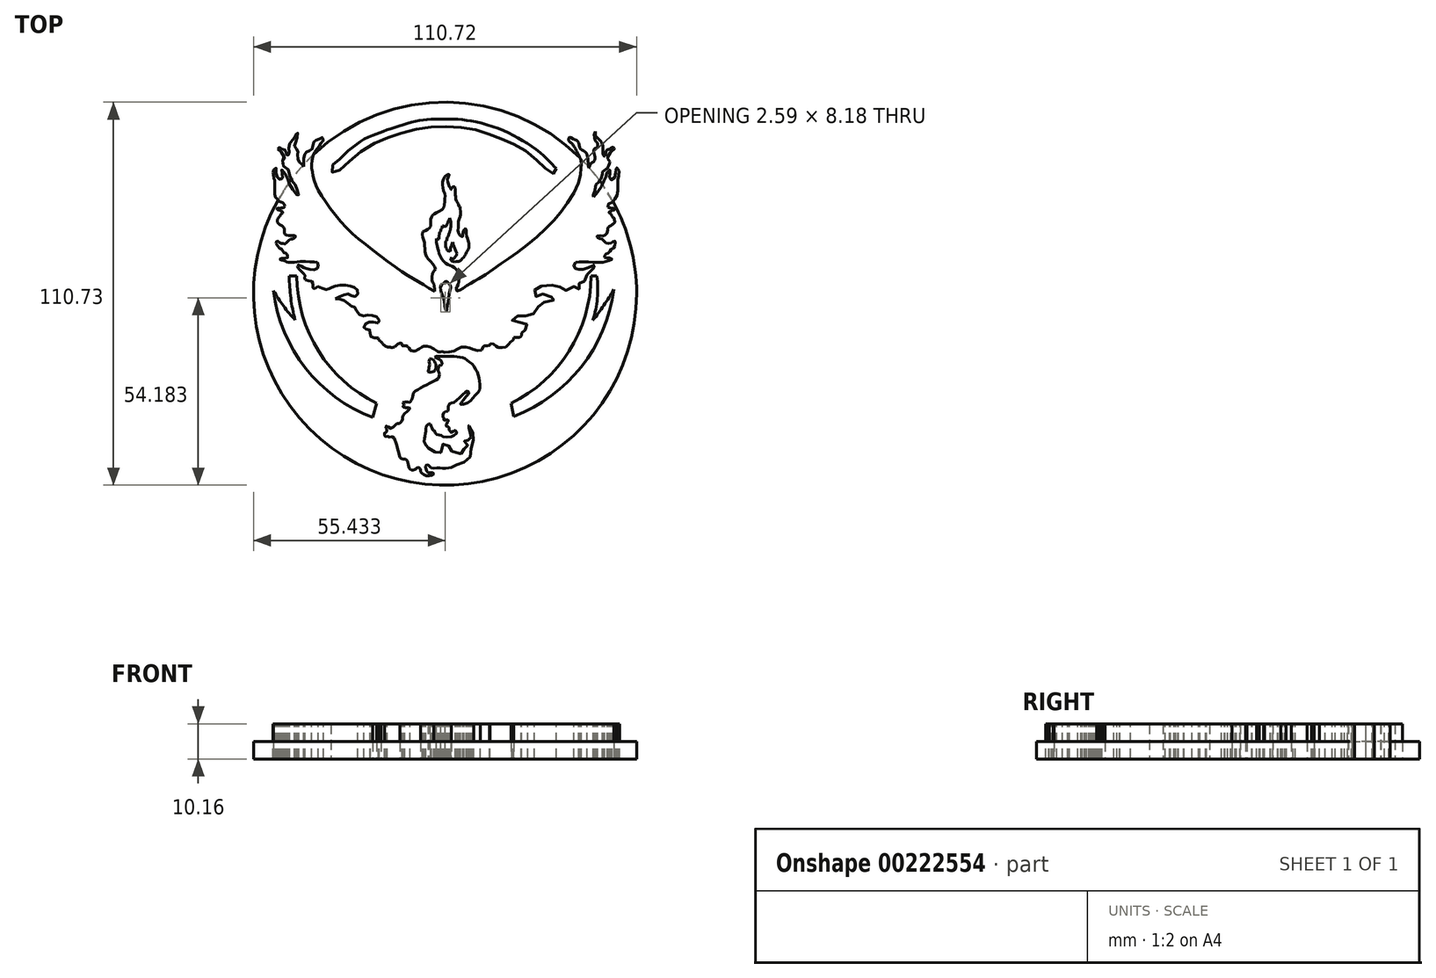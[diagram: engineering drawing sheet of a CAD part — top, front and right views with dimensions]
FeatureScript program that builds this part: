
annotation { "Feature Type Name" : "Feature", "Feature Type Description" : "" }
export const myFeature = defineFeature(function(context is Context, id is Id, definition is map)
    precondition{}
    {
        {
            var Q0;
            Q0=qCreatedBy(makeId("Top.planeOp"),FACE);
            var sketch = newSketch(context, id + "F0", { "sketchPlane" : qUnion([Q0])});
            skFitSpline(sketch, "E0", {"points": [v(-16.86, -5.52) * mm, v(-16.94, -4.58) * mm, v(-17.18, -3.24) * mm, v(-17.57, -2.77) * mm, v(-17.73, -1.5) * mm, v(-17.34, 0) * mm, v(-16.7, 0.77) * mm, v(-17.26, 2.2) * mm, v(-18.52, 3.53) * mm, v(-19.3, 4.55) * mm, v(-19.7, 5.97) * mm, v(-19.78, 7.54) * mm, v(-20.01, 9.12) * mm, v(-20.4, 10.3) * mm, v(-20.4, 11.71) * mm], "startDerivative": vector(-1.27, 14.06) * mm, "endDerivative": vector(1.69, 19.9) * mm});
            skFitSpline(sketch, "E1", {"points": [v(-20.4, 11.71) * mm, v(-18.83, 12.42) * mm, v(-18.12, 13.2) * mm, v(-18.04, 14.47) * mm, v(-17.89, 15.8) * mm, v(-17.42, 16.6) * mm, v(-16.08, 17.38) * mm, v(-14.35, 18.56) * mm, v(-14.03, 20.52) * mm, v(-13.95, 22.41) * mm, v(-14.5, 24.14) * mm, v(-14.58, 26.03) * mm], "startDerivative": vector(17.95, 6.85) * mm, "endDerivative": vector(1, 19.32) * mm});
            skFitSpline(sketch, "E2", {"points": [v(-14.58, 26.03) * mm, v(-14.35, 27.05) * mm, v(-13.54, 28) * mm, v(-12.72, 28.29) * mm, v(-12.8, 27.75) * mm, v(-13.23, 26.9) * mm, v(-13.17, 26.03) * mm, v(-12.8, 25.33) * mm, v(-12.78, 24.77) * mm, v(-12.4, 24.48) * mm, v(-12.3, 24.09) * mm, v(-12.07, 23.86) * mm, v(-11.87, 24.43) * mm, v(-11.6, 24.74) * mm, v(-11.17, 24.74) * mm, v(-10.97, 24.12) * mm, v(-11, 23.24) * mm, v(-10.89, 22.4) * mm, v(-10.8, 21.61) * mm, v(-10.8, 21.02) * mm, v(-10.47, 20.31) * mm, v(-9.96, 19.47) * mm, v(-9.85, 18.96) * mm, v(-9.48, 18.96) * mm], "startDerivative": vector(2.4, 19.07) * mm, "endDerivative": vector(13.83, 3.06) * mm});
            skFitSpline(sketch, "E3", {"points": [v(-9.48, 18.96) * mm, v(-9.48, 17.82) * mm, v(-9.48, 16.19) * mm, v(-9.9, 15.18) * mm, v(-10.1, 13.3) * mm, v(-10.1, 11.71) * mm, v(-9.48, 10.56) * mm, v(-8.8, 10.27) * mm, v(-8.8, 11.23) * mm, v(-8.36, 12.1) * mm, v(-8.02, 12.58) * mm, v(-7.78, 12.15) * mm, v(-7.78, 11.23) * mm, v(-7.54, 9.89) * mm, v(-7.2, 9.17) * mm], "startDerivative": vector(-0.48, -14.29) * mm, "endDerivative": vector(5.74, -10.35) * mm});
            skFitSpline(sketch, "E4", {"points": [v(-7.2, 9.17) * mm, v(-7.03, 8.35) * mm, v(-6.96, 7.49) * mm, v(-7.2, 6.6) * mm, v(-7.65, 5.86) * mm, v(-7.92, 5.3) * mm, v(-8.3, 4.6) * mm, v(-8.82, 3.99) * mm, v(-9.48, 3.35) * mm, v(-10.89, 3.01) * mm, v(-11.95, 3.25) * mm, v(-12.4, 3.97) * mm], "startDerivative": vector(2.2, -9.22) * mm, "endDerivative": vector(-4.07, 9.3) * mm});
            skFitSpline(sketch, "E5", {"points": [v(-12.4, 3.97) * mm, v(-11.32, 3.97) * mm, v(-10.84, 4.6) * mm, v(-10.47, 5.41) * mm, v(-10.99, 6.52) * mm, v(-11.51, 8.05) * mm, v(-11.66, 8.63) * mm], "startDerivative": vector(7.19, -1.15) * mm, "endDerivative": vector(-0.95, 3.88) * mm});
            skFitSpline(sketch, "E6", {"points": [v(-11.66, 8.63) * mm, v(-12.01, 7.92) * mm, v(-12.22, 7.4) * mm, v(-12.34, 6.78) * mm, v(-12.36, 6.25) * mm, v(-12.5, 6.03) * mm, v(-12.81, 6.1) * mm, v(-13.04, 6.13) * mm, v(-13.44, 6.8) * mm, v(-13.7, 7.44) * mm, v(-13.71, 8.3) * mm, v(-13.71, 8.87) * mm, v(-13.56, 8.98) * mm, v(-13.37, 9.47) * mm, v(-13.2, 9.97) * mm, v(-13.06, 10.22) * mm], "startDerivative": vector(-4.49, -8.8) * mm, "endDerivative": vector(2.8, 4.47) * mm});
            skFitSpline(sketch, "E7", {"points": [v(-13.06, 10.22) * mm, v(-12.55, 11.7) * mm, v(-12.27, 12.87) * mm, v(-12.27, 14.63) * mm, v(-12.55, 15.6) * mm], "startDerivative": vector(2.1, 5.8) * mm, "endDerivative": vector(-1.53, 4.03) * mm});
            skFitSpline(sketch, "E8", {"points": [v(-12.55, 15.6) * mm, v(-13.06, 14.53) * mm, v(-13.65, 13.29) * mm, v(-14.14, 13.29) * mm, v(-14.62, 13.32) * mm], "startDerivative": vector(-1.78, -3.18) * mm, "endDerivative": vector(-2.5, 0.02) * mm});
            skFitSpline(sketch, "E9", {"points": [v(-14.62, 13.32) * mm, v(-14.96, 12.42) * mm, v(-15.45, 11.45) * mm, v(-15.59, 10.66) * mm, v(-15.66, 9.93) * mm, v(-15.66, 9.62) * mm, v(-16.07, 9.59) * mm, v(-16.38, 9.66) * mm], "startDerivative": vector(-1.66, -5.03) * mm, "endDerivative": vector(-2.66, 0.75) * mm});
            skFitSpline(sketch, "E10", {"points": [v(-16.38, 9.66) * mm, v(-16.38, 8.95) * mm, v(-16.3, 8.08) * mm, v(-16.12, 7.17) * mm, v(-15.7, 5.74) * mm, v(-15, 3.97) * mm, v(-13.7, 2.58) * mm, v(-12.4, 1.88) * mm, v(-11.28, 1.42) * mm, v(-10.12, 0) * mm, v(-9.84, -0.78) * mm, v(-9.84, -2.49) * mm, v(-10.4, -4.2) * mm], "startDerivative": vector(-0.3, -11.43) * mm, "endDerivative": vector(-6.96, -16.94) * mm});
            skFitSpline(sketch, "E11", {"points": [v(-10.4, -4.2) * mm, v(-10.6, -4.39) * mm, v(-10.66, -4.94) * mm, v(-10.4, -5.38) * mm, v(-10.18, -5.49) * mm, v(-9.52, -5.12) * mm, v(-8.76, -4.67) * mm, v(-7.82, -3.98) * mm, v(-6.53, -3.27) * mm, v(-5.6, -2.64) * mm, v(-3.44, -1.53) * mm, v(1.05, 1.62) * mm, v(6.8, 5.57) * mm, v(14.8, 12.13) * mm, v(20.46, 18.5) * mm, v(24.77, 26.05) * mm, v(25.4, 30.18) * mm], "startDerivative": vector(-10.46, -6.9) * mm, "endDerivative": vector(1.76, 47.56) * mm});
            skFitSpline(sketch, "E12", {"points": [v(25.4, 30.18) * mm, v(25.4, 32.23) * mm, v(24.15, 34.94) * mm, v(23.08, 36.75) * mm, v(21.78, 38.05) * mm], "startDerivative": vector(1.08, 8.26) * mm, "endDerivative": vector(-6.03, 5.72) * mm});
            skFitSpline(sketch, "E13", {"points": [v(21.78, 38.05) * mm, v(22.08, 39.01) * mm, v(23.23, 38.42) * mm, v(24.3, 38.05) * mm, v(24.82, 37.12) * mm, v(25.08, 35.83) * mm, v(25.93, 35.16) * mm, v(26.86, 34.53) * mm, v(27.26, 33.34) * mm, v(27.49, 31.94) * mm, v(27.52, 30.94) * mm, v(27.7, 30.18) * mm], "startDerivative": vector(1.63, 15.2) * mm, "endDerivative": vector(3.06, -9.7) * mm});
            skFitSpline(sketch, "E14", {"points": [v(27.7, 30.18) * mm, v(28.26, 31.42) * mm, v(28.97, 31.86) * mm, v(29.34, 32.5) * mm, v(29.38, 33.38) * mm, v(29.15, 34.27) * mm, v(29.08, 34.94) * mm, v(29.38, 35.79) * mm, v(30, 35.9) * mm, v(30.26, 36.57) * mm, v(30.04, 37.5) * mm, v(29.52, 38.05) * mm, v(29.23, 39.68) * mm, v(29.6, 40.68) * mm], "startDerivative": vector(4.58, 15.51) * mm, "endDerivative": vector(5.9, 10.64) * mm});
            skFitSpline(sketch, "E15", {"points": [v(29.6, 40.68) * mm, v(29.6, 39.57) * mm, v(30.26, 38.71) * mm, v(30.93, 38.05) * mm, v(31.6, 37.01) * mm, v(31.75, 35.64) * mm, v(31.67, 34.82) * mm, v(31.75, 34.34) * mm, v(31.93, 33.64) * mm, v(32.3, 33.53) * mm], "startDerivative": vector(-1.31, -9.25) * mm, "endDerivative": vector(5.74, -0.16) * mm});
            skFitSpline(sketch, "E16", {"points": [v(32.3, 33.53) * mm, v(32.52, 34.2) * mm, v(32.64, 34.92) * mm, v(32.91, 35.39) * mm, v(33.38, 35.4) * mm, v(33.93, 35.58) * mm, v(34.15, 35.97) * mm, v(34.67, 36.1) * mm, v(35.08, 35.73) * mm, v(34.68, 35.3) * mm, v(33.93, 34.7) * mm, v(33.4, 33.74) * mm, v(33.05, 33.15) * mm, v(33.17, 32.67) * mm, v(33.6, 32.22) * mm, v(33.74, 31.64) * mm, v(33.48, 30.97) * mm, v(33.1, 30.38) * mm, v(33.08, 29.95) * mm, v(32.77, 29.92) * mm, v(32.3, 29.5) * mm, v(31.6, 28.97) * mm], "startDerivative": vector(4.9, 12.98) * mm, "endDerivative": vector(-13.3, -8.7) * mm});
            skFitSpline(sketch, "E17", {"points": [v(31.6, 28.97) * mm, v(31.6, 28.25) * mm, v(31.22, 27.1) * mm, v(30.93, 26.64) * mm, v(30.48, 26.05) * mm, v(29.74, 25.3) * mm, v(29.63, 24.77) * mm, v(29.46, 23.75) * mm, v(29.26, 23.07) * mm, v(28.95, 22.13) * mm, v(29, 21.77) * mm], "startDerivative": vector(0.7, -6.71) * mm, "endDerivative": vector(1.6, -4.57) * mm});
            skFitSpline(sketch, "E18", {"points": [v(29, 21.77) * mm, v(29.98, 22.85) * mm, v(31.01, 24.31) * mm, v(31.82, 25.62) * mm, v(32, 26.42) * mm, v(32.38, 27.1) * mm, v(32.72, 27.98) * mm, v(32.81, 28.7) * mm, v(33.16, 28.97) * mm, v(33.56, 29.47) * mm, v(33.87, 29.47) * mm, v(33.84, 29.16) * mm, v(33.8, 28.6) * mm, v(33.68, 27.92) * mm, v(33.68, 27.17) * mm, v(33.75, 26.7) * mm, v(34.27, 26.74) * mm, v(34.74, 27.2) * mm, v(35.18, 27.39) * mm, v(35.4, 28.29) * mm, v(35.4, 29.1) * mm, v(35.58, 29.4) * mm, v(35.42, 30.1) * mm, v(35.46, 30.43) * mm, v(35.83, 30.03) * mm, v(36.1, 29.4) * mm, v(36.42, 29.13) * mm, v(36.42, 28.2) * mm, v(36.17, 27.6) * mm, v(36.17, 26.9) * mm, v(35.92, 26.49) * mm, v(35.98, 25.46) * mm, v(35.98, 24.31) * mm, v(36.02, 22.76) * mm, v(35.8, 22.13) * mm, v(35.77, 21.77) * mm, v(35.27, 21.17) * mm, v(34.7, 20.7) * mm, v(34.5, 20.27) * mm, v(34, 20.24) * mm, v(33.28, 19.74) * mm, v(33.03, 19.24) * mm, v(33.16, 18.75) * mm], "startDerivative": vector(28.84, 29.63) * mm, "endDerivative": vector(9.8, -24.72) * mm});
            skFitSpline(sketch, "E19", {"points": [v(33.16, 18.75) * mm, v(33.6, 18.61) * mm, v(34.2, 18.5) * mm, v(34.76, 18.52) * mm, v(35.12, 18.48) * mm, v(35.16, 18.26) * mm, v(34.77, 17.9) * mm, v(34.42, 17.88) * mm, v(34.13, 17.7) * mm, v(33.72, 17.5) * mm, v(33.54, 17.27) * mm, v(33.64, 17.06) * mm, v(33.98, 16.93) * mm, v(34.18, 16.7) * mm], "startDerivative": vector(5.08, -1.62) * mm, "endDerivative": vector(2.28, -3.99) * mm});
            skFitSpline(sketch, "E20", {"points": [v(34.18, 16.7) * mm, v(34.36, 16.24) * mm, v(34.41, 16) * mm, v(34.76, 15.72) * mm, v(35.07, 15.48) * mm, v(35.07, 14.92) * mm, v(35.27, 14.5) * mm, v(34.76, 14.02) * mm, v(34.18, 13.51) * mm, v(33.49, 13.15) * mm, v(33.16, 12.61) * mm, v(33.16, 12.05) * mm], "startDerivative": vector(2.74, -5.6) * mm, "endDerivative": vector(0.66, -6.02) * mm});
            skFitSpline(sketch, "E21", {"points": [v(33.16, 12.05) * mm, v(32.7, 10.9) * mm, v(31.8, 10.52) * mm, v(30.7, 10.56) * mm, v(29.95, 10.33) * mm, v(30.56, 9.8) * mm, v(31.51, 9.52) * mm, v(32.27, 8.76) * mm, v(33.16, 8.3) * mm, v(34.18, 8.48) * mm, v(34.76, 8.86) * mm, v(35.27, 8.95) * mm, v(35.27, 8.05) * mm, v(34.76, 6.92) * mm, v(34.18, 6.68) * mm, v(33.6, 5.78) * mm, v(32.7, 5.35) * mm, v(32.27, 4.88) * mm, v(32.22, 4.17) * mm], "startDerivative": vector(-4.75, -20.24) * mm, "endDerivative": vector(0.74, -15.16) * mm});
            skFitSpline(sketch, "E22", {"points": [v(32.22, 4.17) * mm, v(32.64, 4.3) * mm, v(32.89, 4.12) * mm, v(33.47, 4.12) * mm, v(34.18, 4.03) * mm, v(34.37, 3.74) * mm, v(33.64, 3.34) * mm, v(32.85, 3.16) * mm, v(32.34, 2.88) * mm, v(31.32, 2.82) * mm, v(29.46, 2.84) * mm, v(28, 2.95) * mm, v(26.79, 2.97) * mm, v(25.47, 2.99) * mm, v(24.26, 2.93) * mm, v(23.63, 2.63) * mm, v(23.32, 1.74) * mm, v(23.7, 1.07) * mm, v(24.7, 0.75) * mm, v(26.01, 0.86) * mm, v(27.16, 1.13) * mm, v(28.08, 1.57) * mm, v(28.81, 1.86) * mm, v(29.17, 2) * mm, v(29.19, 1.44) * mm, v(28.46, 0.6) * mm, v(27.96, 0) * mm, v(27.29, -0.4) * mm, v(27.1, -0.77) * mm], "startDerivative": vector(17.9, 9.8) * mm, "endDerivative": vector(-4.25, -15.98) * mm});
            skFitSpline(sketch, "E23", {"points": [v(27.1, -0.77) * mm, v(27.1, -1.72) * mm, v(26.67, -2.35) * mm, v(25.57, -2.78) * mm, v(25.04, -2.68) * mm, v(24.84, -3.4) * mm, v(24.75, -4.27) * mm, v(25.08, -4.66) * mm, v(24.41, -4.95) * mm, v(23.98, -4.22) * mm, v(23.4, -4.13) * mm, v(22.3, -5.04) * mm, v(21.14, -5.28) * mm, v(20.03, -4.8) * mm, v(19.55, -4.42) * mm, v(18.44, -3.89) * mm, v(17.58, -3.8) * mm, v(16.18, -3.74) * mm, v(14.16, -3.98) * mm, v(12.9, -4.37) * mm, v(12.1, -4.95) * mm, v(11.95, -6.05) * mm, v(12.1, -6.63) * mm, v(12.62, -7.16) * mm, v(13.73, -6.73) * mm, v(14.3, -6.34) * mm, v(15.6, -6.53) * mm, v(17.2, -7.4) * mm, v(18.25, -8.03) * mm, v(16.85, -8.07) * mm, v(15.46, -8.31) * mm, v(14.16, -9.13) * mm, v(13.68, -9.57) * mm, v(12.96, -10.1) * mm, v(12.23, -11.1) * mm, v(11.6, -12.07) * mm, v(10.21, -12.65) * mm, v(9.25, -12.7) * mm, v(8.05, -12.5) * mm, v(7.04, -12.74) * mm, v(6.36, -13.32) * mm, v(5.54, -13.7) * mm, v(5.93, -14.72) * mm, v(6.9, -14.52) * mm, v(8.2, -14.38) * mm, v(9.5, -14.81) * mm, v(10.02, -15.92) * mm, v(9.88, -16.54) * mm, v(8.87, -16.64) * mm, v(8.1, -16.69) * mm, v(8.24, -17.6) * mm], "startDerivative": vector(4.98, -52.78) * mm, "endDerivative": vector(20.93, -60.42) * mm});
            skFitSpline(sketch, "E24", {"points": [v(8.24, -17.6) * mm, v(8.24, -18.16) * mm, v(7.84, -18.73) * mm, v(6.85, -18.91) * mm, v(5.93, -18.89) * mm], "startDerivative": vector(0.31, -2.6) * mm, "endDerivative": vector(-3.27, 0.16) * mm});
            skFitSpline(sketch, "E25", {"points": [v(5.93, -18.89) * mm, v(5.93, -19.49) * mm, v(5.26, -19.85) * mm, v(4.82, -20.48) * mm, v(4.17, -21.18) * mm, v(3.28, -21.83) * mm, v(2.26, -21.83) * mm, v(1.35, -21.8) * mm, v(0.78, -21.34) * mm, v(0.26, -20.87) * mm, v(-0.5, -20.69) * mm, v(-1, -20.74) * mm, v(-0.97, -21.1) * mm, v(-1.3, -21.34) * mm, v(-2.2, -21.29) * mm, v(-2.61, -21.36) * mm, v(-2.8, -21.62) * mm, v(-3.03, -21.7) * mm, v(-3.38, -22.61) * mm, v(-4.85, -22.61) * mm, v(-6.25, -22.23) * mm, v(-6.94, -21.85) * mm, v(-8.47, -21.6) * mm, v(-9.61, -21.79) * mm, v(-10.82, -22.55) * mm, v(-12.54, -23.06) * mm, v(-13.94, -23.18) * mm], "startDerivative": vector(5.13, -21.26) * mm, "endDerivative": vector(-27.28, -1.54) * mm});
            skFitSpline(sketch, "E26", {"points": [v(18.24, 30) * mm, v(16.85, 31.38) * mm, v(13.79, 34.37) * mm, v(8.24, 38.17) * mm, v(2.1, 41.31) * mm, v(-5.35, 43.5) * mm, v(-10.18, 44.24) * mm], "startDerivative": vector(-12.55, 12.25) * mm, "endDerivative": vector(-27.98, 3.35) * mm});
            skFitSpline(sketch, "E27", {"points": [v(-10.18, 44.24) * mm, v(-17.52, 44.24) * mm, v(-21.6, 43.8) * mm, v(-26.13, 42.55) * mm, v(-30.4, 41.23) * mm, v(-33.87, 39.87) * mm, v(-38.43, 37.82) * mm], "startDerivative": vector(-38.77, 0.5) * mm, "endDerivative": vector(-27.3, -16.6) * mm});
            skFitSpline(sketch, "E28", {"points": [v(-38.43, 37.82) * mm, v(-43.44, 33.67) * mm, v(-45.42, 31.68) * mm, v(-46.83, 30.18) * mm, v(-46.27, 28.67) * mm, v(-43.81, 29.99) * mm, v(-39.57, 33.76) * mm, v(-33.15, 37.82) * mm, v(-27.4, 39.9) * mm, v(-20.7, 41.59) * mm, v(-13.91, 42.06) * mm, v(-7.12, 41.59) * mm, v(-1.27, 39.99) * mm, v(3.92, 37.82) * mm, v(8.92, 35.46) * mm, v(13.35, 31.68) * mm, v(16.18, 29.14) * mm, v(17.78, 28.57) * mm, v(18.24, 30) * mm], "startDerivative": vector(-87.21, -57.5) * mm, "endDerivative": vector(6.34, 58.2) * mm});
            skFitSpline(sketch, "E29", {"points": [v(-13.94, -23.18) * mm, v(-14.86, -23) * mm, v(-15.8, -23) * mm, v(-16.37, -22.69) * mm, v(-17.35, -22.09) * mm, v(-18.36, -21.6) * mm, v(-19.4, -21.43) * mm, v(-19.9, -21.4) * mm, v(-20.75, -21.86) * mm, v(-21.73, -22.39) * mm, v(-22.69, -22.77) * mm, v(-23.53, -22.72) * mm], "startDerivative": vector(-9.74, 2.84) * mm, "endDerivative": vector(-9.64, 1.67) * mm});
            skFitSpline(sketch, "E30", {"points": [v(-23.53, -22.72) * mm, v(-24.1, -22.54) * mm, v(-24.18, -22.11) * mm, v(-24.3, -21.77) * mm, v(-24.64, -21.77) * mm, v(-24.69, -21.45) * mm, v(-24.92, -21.34) * mm, v(-25.8, -21.35) * mm, v(-26.34, -21.26) * mm, v(-26.29, -20.81) * mm], "startDerivative": vector(-5.43, 0.74) * mm, "endDerivative": vector(1.54, 4.76) * mm});
            skFitSpline(sketch, "E31", {"points": [v(-26.29, -20.81) * mm, v(-26.78, -20.58) * mm, v(-27.8, -21) * mm, v(-28.53, -21.63) * mm, v(-29.55, -21.75) * mm, v(-30.87, -21.54) * mm, v(-31.84, -20.81) * mm, v(-32.43, -20.02) * mm], "startDerivative": vector(-4.1, 3.18) * mm, "endDerivative": vector(-3.81, 5.64) * mm});
            skFitSpline(sketch, "E32", {"points": [v(-32.43, -20.02) * mm, v(-33.07, -19.58) * mm, v(-33.1, -19) * mm], "startDerivative": vector(-1.5, 0.71) * mm, "endDerivative": vector(0.19, 1.34) * mm});
            skFitSpline(sketch, "E33", {"points": [v(-33.1, -19) * mm, v(-34.57, -19) * mm, v(-35.54, -18.42) * mm, v(-35.48, -17.03) * mm, v(-35.96, -16.54) * mm, v(-37.28, -16.33) * mm, v(-37.21, -15.3) * mm, v(-36.1, -14.46) * mm, v(-34.85, -14.46) * mm, v(-33.1, -14.67) * mm, v(-33.1, -13.56) * mm, v(-34.5, -12.58) * mm, v(-36.1, -12.44) * mm, v(-37.9, -12.65) * mm, v(-39.3, -11.54) * mm, v(-39.99, -10.15) * mm, v(-40.82, -9.87) * mm, v(-42.42, -8.7) * mm, v(-43.8, -7.93) * mm, v(-45.62, -7.72) * mm], "startDerivative": vector(-27.39, -2.24) * mm, "endDerivative": vector(-31.84, 1.41) * mm});
            skFitSpline(sketch, "E34", {"points": [v(-45.62, -7.72) * mm, v(-43.4, -6.68) * mm, v(-41.66, -6.33) * mm, v(-40.34, -7.03) * mm, v(-39.3, -6.6) * mm, v(-39.3, -5.01) * mm, v(-40.82, -4.18) * mm, v(-43.05, -3.76) * mm, v(-45.62, -4.04) * mm, v(-46.93, -4.53) * mm, v(-47.7, -4.94) * mm, v(-49.02, -4.94) * mm, v(-50.9, -4.18) * mm, v(-51.87, -4.94) * mm, v(-52.07, -3.7) * mm, v(-52.28, -2.72) * mm, v(-53.19, -2.58) * mm, v(-54.23, -2.23) * mm], "startDerivative": vector(29.87, 14.57) * mm, "endDerivative": vector(-19.98, 8.99) * mm});
            skFitSpline(sketch, "E35", {"points": [v(-54.23, -2.23) * mm, v(-54.47, -1.81) * mm, v(-54.43, -1.26) * mm, v(-54.5, -0.57) * mm, v(-54.89, -0.33) * mm, v(-55.25, 0) * mm, v(-55.67, 0.46) * mm, v(-56.26, 1.05) * mm, v(-56.54, 1.6) * mm, v(-56.47, 2.06) * mm, v(-55.63, 1.83) * mm, v(-54.83, 1.3) * mm, v(-54.03, 1.03) * mm, v(-52.77, 0.78) * mm, v(-51.11, 0.9) * mm, v(-50.56, 1.87) * mm, v(-50.9, 2.84) * mm, v(-52.16, 3) * mm, v(-54.03, 3.05) * mm, v(-56.24, 3.05) * mm, v(-56.98, 2.82) * mm, v(-58.68, 2.82) * mm], "startDerivative": vector(-9.07, 11.9) * mm, "endDerivative": vector(-30.21, 1.95) * mm});
            skFitSpline(sketch, "E36", {"points": [v(-58.68, 2.82) * mm, v(-59.48, 2.93) * mm, v(-60.08, 3.15) * mm, v(-60.47, 3.32) * mm, v(-61.26, 3.5) * mm, v(-61.57, 3.65) * mm, v(-61.49, 3.9) * mm, v(-60.87, 3.97) * mm, v(-60.17, 4) * mm, v(-59.85, 4.19) * mm, v(-59.45, 4.16) * mm, v(-59.43, 4.81) * mm, v(-59.74, 5.29) * mm, v(-60.46, 5.67) * mm, v(-60.78, 5.95) * mm, v(-60.96, 6.39) * mm, v(-61.3, 6.78) * mm, v(-61.8, 6.84) * mm, v(-61.95, 7.16) * mm, v(-62.13, 7.37) * mm, v(-62.26, 7.5) * mm], "startDerivative": vector(-12.7, 1.25) * mm, "endDerivative": vector(-3.95, 4.14) * mm});
            skFitSpline(sketch, "E37", {"points": [v(-62.26, 7.5) * mm, v(-62.4, 7.82) * mm, v(-62.67, 8.06) * mm, v(-62.71, 8.46) * mm, v(-62.6, 8.93) * mm, v(-62.07, 8.89) * mm, v(-61.59, 8.45) * mm, v(-61.1, 8.26) * mm, v(-60.71, 8.3) * mm, v(-60.23, 8.16) * mm, v(-59.62, 8.64) * mm, v(-58.83, 9.4) * mm, v(-58.35, 9.57) * mm, v(-57.9, 9.6) * mm, v(-57.3, 10.04) * mm, v(-57.12, 10.49) * mm, v(-57.99, 10.64) * mm, v(-59.02, 10.64) * mm, v(-59.72, 10.65) * mm, v(-60.12, 10.9) * mm, v(-60.32, 11.33) * mm, v(-60.36, 11.96) * mm, v(-60.36, 12.31) * mm, v(-60.4, 12.56) * mm, v(-60.54, 12.95) * mm], "startDerivative": vector(-3.04, 10.53) * mm, "endDerivative": vector(-4.1, 11.48) * mm});
            skFitSpline(sketch, "E38", {"points": [v(-60.54, 12.95) * mm, v(-61.04, 13.4) * mm, v(-61.79, 13.8) * mm, v(-62.19, 14.21) * mm, v(-62.38, 14.4) * mm, v(-62.4, 14.66) * mm, v(-62.4, 15.04) * mm, v(-62.24, 15.45) * mm, v(-61.88, 15.85) * mm, v(-61.61, 16.08) * mm], "startDerivative": vector(-3.27, 3.65) * mm, "endDerivative": vector(2.56, 2.25) * mm});
            skFitSpline(sketch, "E39", {"points": [v(-61.61, 16.08) * mm, v(-61.61, 16.44) * mm, v(-61.27, 16.8) * mm, v(-60.92, 16.97) * mm, v(-60.79, 17.34) * mm, v(-61.12, 17.6) * mm, v(-61.42, 17.72) * mm, v(-61.61, 17.91) * mm, v(-62.05, 17.9) * mm, v(-62.45, 18.2) * mm, v(-62.32, 18.5) * mm, v(-61.61, 18.5) * mm, v(-60.96, 18.6) * mm, v(-60.4, 18.72) * mm, v(-60.29, 19.3) * mm, v(-60.54, 19.8) * mm, v(-61.08, 20.18) * mm, v(-61.48, 20.3) * mm, v(-61.9, 20.55) * mm], "startDerivative": vector(-1.38, 7.32) * mm, "endDerivative": vector(-7.32, 5.24) * mm});
            skFitSpline(sketch, "E40", {"points": [v(-61.9, 20.55) * mm, v(-62.2, 20.92) * mm, v(-62.63, 21.4) * mm, v(-62.88, 21.55) * mm, v(-63, 21.9) * mm], "startDerivative": vector(-1.14, 1.28) * mm, "endDerivative": vector(-0.26, 1.84) * mm});
            skFitSpline(sketch, "E41", {"points": [v(-63, 21.9) * mm, v(-63.1, 22.2) * mm, v(-63.17, 23.46) * mm, v(-63.16, 25.51) * mm, v(-63.1, 26.48) * mm, v(-63.26, 26.72) * mm, v(-63.36, 27.2) * mm, v(-63.47, 27.84) * mm, v(-63.56, 28.24) * mm, v(-63.56, 29.04) * mm, v(-63.35, 29.6) * mm], "startDerivative": vector(-1.95, 3.68) * mm, "endDerivative": vector(2.85, 5.49) * mm});
            skFitSpline(sketch, "E42", {"points": [v(-63.35, 29.6) * mm, v(-62.97, 30.26) * mm, v(-62.72, 30.33) * mm, v(-62.77, 29.6) * mm, v(-62.63, 29.04) * mm, v(-62.7, 28.24) * mm, v(-62.38, 27.84) * mm, v(-62.4, 27.48) * mm, v(-61.9, 27.43) * mm, v(-61.9, 27.16) * mm, v(-61.53, 26.72) * mm, v(-60.9, 26.72) * mm, v(-60.92, 27.33) * mm, v(-60.87, 27.84) * mm, v(-60.94, 28.24) * mm, v(-61.02, 29.04) * mm, v(-61.29, 29.26) * mm, v(-61.11, 29.6) * mm, v(-60.4, 29.04) * mm, v(-59.97, 28.04) * mm, v(-59.58, 27.11) * mm, v(-59.26, 26.65) * mm, v(-59.29, 26.09) * mm, v(-58.8, 25.43) * mm, v(-58.26, 24.4) * mm, v(-57.4, 23.26) * mm, v(-56.75, 22.38) * mm, v(-56.29, 21.9) * mm, v(-56.16, 22.18) * mm, v(-56.46, 22.57) * mm, v(-56.6, 23.38) * mm, v(-56.8, 24.18) * mm, v(-56.94, 24.99) * mm, v(-57.43, 25.55) * mm, v(-58.04, 26.35) * mm, v(-58.43, 26.62) * mm, v(-58.87, 27.84) * mm, v(-58.82, 28.62) * mm, v(-59.26, 29.6) * mm, v(-60.14, 30.11) * mm, v(-60.7, 30.87) * mm, v(-61.04, 31.72) * mm, v(-60.65, 32.48) * mm, v(-60.29, 33.06) * mm, v(-60.65, 33.7) * mm, v(-60.94, 34.3) * mm, v(-61.43, 34.82) * mm, v(-61.9, 35.23) * mm, v(-62.21, 35.55) * mm], "startDerivative": vector(14.73, 35.5) * mm, "endDerivative": vector(-18.28, 18.47) * mm});
            skFitSpline(sketch, "E43", {"points": [v(-62.21, 35.55) * mm, v(-62.1, 35.92) * mm, v(-61.71, 36.06) * mm, v(-61.11, 35.76) * mm, v(-61.11, 35.55) * mm, v(-60.4, 35.45) * mm, v(-59.88, 35) * mm, v(-59.85, 34.41) * mm, v(-59.62, 34.08) * mm, v(-59.57, 33.7) * mm, v(-59.22, 33.7) * mm, v(-59.12, 34.18) * mm, v(-58.96, 34.53) * mm, v(-59.05, 35.03) * mm, v(-59.07, 36.49) * mm, v(-58.67, 37.4) * mm, v(-57.94, 38.23) * mm, v(-57.4, 38.89) * mm, v(-56.93, 39.45) * mm, v(-56.9, 40.16) * mm, v(-56.6, 40.32) * mm, v(-56.56, 39.45) * mm, v(-56.74, 38.3) * mm, v(-57.3, 37.2) * mm, v(-57.45, 36.27) * mm, v(-57.05, 35.83) * mm, v(-56.58, 35.55) * mm, v(-56.34, 34.44) * mm, v(-56.48, 34.08) * mm, v(-56.48, 32.95) * mm, v(-56.34, 32.32) * mm, v(-55.92, 31.73) * mm, v(-55.61, 31.59) * mm, v(-55.21, 30.9) * mm, v(-54.77, 30.55) * mm], "startDerivative": vector(2.06, 18.3) * mm, "endDerivative": vector(17.48, -9.47) * mm});
            skFitSpline(sketch, "E44", {"points": [v(-54.77, 30.55) * mm, v(-54.77, 32.2) * mm, v(-54.39, 34.16) * mm, v(-53.68, 34.96) * mm, v(-52.5, 35.45) * mm, v(-52.06, 36.6) * mm, v(-51.63, 37.88) * mm, v(-50.62, 38.3) * mm, v(-49.4, 38.96) * mm, v(-49.2, 38.49) * mm, v(-49.02, 38.16) * mm, v(-49.63, 37.52) * mm, v(-50.39, 36.35) * mm, v(-51.33, 35.17) * mm, v(-52.15, 33.38) * mm, v(-52.53, 31.24) * mm, v(-52.39, 29.6) * mm, v(-52.06, 27.84) * mm], "startDerivative": vector(-0.91, 23.81) * mm, "endDerivative": vector(5.14, -26.17) * mm});
            skFitSpline(sketch, "E45", {"points": [v(-52.06, 27.84) * mm, v(-51.05, 24.69) * mm, v(-48.02, 19.8) * mm, v(-42.26, 12.67) * mm, v(-34.73, 6.31) * mm, v(-26.13, 0) * mm, v(-21.53, -2.88) * mm, v(-16.86, -5.52) * mm], "startDerivative": vector(7.65, -30.8) * mm, "endDerivative": vector(37.83, -21.2) * mm});
            skFitSpline(sketch, "E46", {"points": [v(-13.52, -11.49) * mm, v(-13.86, -10.23) * mm, v(-14.03, -9.6) * mm, v(-14.03, -9.14) * mm, v(-14.26, -7.82) * mm, v(-14.55, -7.02) * mm, v(-14.9, -5.99) * mm, v(-15.12, -5.52) * mm, v(-15.18, -3.98) * mm, v(-14.43, -3.27) * mm, v(-13.8, -2.67) * mm, v(-12.94, -3.27) * mm, v(-12.26, -4.18) * mm, v(-12.54, -5.52) * mm, v(-12.89, -7.94) * mm, v(-13.29, -9.94) * mm, v(-13.52, -11.49) * mm]});
            skArc(sketch, "E47", {"start": v(-63.5, -5.43) * mm, "mid": v(-54.23, -27.74) * mm, "end": v(-34.77, -42.05) * mm});
            skArc(sketch, "E48", {"start": v(-63.5, -5.43) * mm, "mid": v(-60.6, -9.78) * mm, "end": v(-57.27, -13.82) * mm});
            skArc(sketch, "E49", {"start": v(-58.92, -1.11) * mm, "mid": v(-58.5, -7.52) * mm, "end": v(-57.27, -13.82) * mm});
            skLineSegment(sketch, "E50", {"start": v(-58.92, -1.11) * mm, "end": v(-56.76, -1.11) * mm});
            skLineSegment(sketch, "E51", {"start": v(-34.77, -42.05) * mm, "end": v(-33.62, -37.98) * mm});
            skArc(sketch, "E52", {"start": v(-56.76, -1.11) * mm, "mid": v(-50.45, -22.85) * mm, "end": v(-33.62, -37.98) * mm});
            skArc(sketch, "E53", {"start": v(5.15, -37.98) * mm, "mid": v(21.96, -22.83) * mm, "end": v(28.33, -1.11) * mm});
            skLineSegment(sketch, "E54", {"start": v(28.33, -1.11) * mm, "end": v(29.99, -1.11) * mm});
            skArc(sketch, "E55", {"start": v(28.83, -13.93) * mm, "mid": v(30.12, -7.58) * mm, "end": v(29.99, -1.11) * mm});
            skArc(sketch, "E56", {"start": v(28.83, -13.93) * mm, "mid": v(32, -9.6) * mm, "end": v(34.87, -5.07) * mm});
            skArc(sketch, "E57", {"start": v(5.98, -41.74) * mm, "mid": v(25.47, -27.38) * mm, "end": v(34.87, -5.07) * mm});
            skLineSegment(sketch, "E58", {"start": v(5.15, -37.98) * mm, "end": v(5.98, -41.74) * mm});
            skFitSpline(sketch, "E59", {"points": [v(-16.97, -24.55) * mm, v(-16.2, -24.38) * mm, v(-14.83, -24.34) * mm, v(-12.62, -24.34) * mm, v(-10.76, -24.38) * mm, v(-9.18, -24.7) * mm, v(-8.2, -24.87) * mm, v(-7.43, -25.57) * mm, v(-6.1, -26.48) * mm, v(-5.19, -27.88) * mm, v(-4.56, -29.04) * mm, v(-4.03, -30.65) * mm, v(-3.82, -32.2) * mm, v(-3.85, -33.98) * mm, v(-4.45, -34.9) * mm], "startDerivative": vector(13.75, 3.93) * mm, "endDerivative": vector(-11.64, -12.72) * mm});
            skFitSpline(sketch, "E60", {"points": [v(-4.45, -34.9) * mm, v(-5.88, -36.5) * mm, v(-7.34, -37.75) * mm, v(-9.4, -38.28) * mm, v(-8.8, -37.29) * mm, v(-7.6, -35.77) * mm, v(-7, -34.9) * mm, v(-7.27, -34.44) * mm, v(-8.2, -34.9) * mm, v(-10.24, -36.83) * mm, v(-11.62, -37.77) * mm, v(-12.44, -37.89) * mm, v(-12.99, -39.02) * mm, v(-13.03, -40.12) * mm, v(-13.85, -40.32) * mm], "startDerivative": vector(-16.92, -18.67) * mm, "endDerivative": vector(-18.7, -0.33) * mm});
            skFitSpline(sketch, "E61", {"points": [v(-13.85, -40.32) * mm, v(-14.19, -40.62) * mm, v(-14.5, -41.28) * mm, v(-14.47, -42) * mm, v(-14.23, -42.2) * mm, v(-14.17, -42.82) * mm, v(-13.58, -42.67) * mm, v(-13.08, -42.7) * mm, v(-13.02, -43.31) * mm, v(-13.25, -43.35) * mm, v(-13.25, -43.81) * mm, v(-13.47, -43.83) * mm, v(-13.58, -44.24) * mm, v(-13.45, -44.65) * mm, v(-13.04, -44.68) * mm, v(-12.78, -44.89) * mm, v(-12.77, -45.62) * mm, v(-12.38, -46.01) * mm, v(-12.06, -46.38) * mm, v(-11.73, -46.01) * mm, v(-11.47, -46.12) * mm, v(-11.03, -45.66) * mm, v(-10.88, -45.98) * mm, v(-10.57, -46.14) * mm, v(-10.47, -46.51) * mm, v(-10.66, -46.68) * mm], "startDerivative": vector(-8.74, -6.47) * mm, "endDerivative": vector(-7.8, -4) * mm});
            skFitSpline(sketch, "E62", {"points": [v(-10.66, -46.68) * mm, v(-11.34, -47.26) * mm, v(-12.7, -47.66) * mm, v(-14.6, -47.54) * mm, v(-15, -47.2) * mm, v(-15.58, -47.11) * mm, v(-16.03, -47.11) * mm, v(-16.53, -46.64) * mm, v(-16.85, -46.13) * mm, v(-16.94, -45.84) * mm, v(-17.44, -45.63) * mm, v(-17.66, -45.17) * mm, v(-17.73, -44.7) * mm, v(-18.14, -44.12) * mm, v(-18.26, -43.78) * mm, v(-18.86, -44.1) * mm, v(-19.46, -44.84) * mm, v(-19.46, -45.58) * mm, v(-19.48, -46.25) * mm, v(-19.62, -46.64) * mm, v(-19.67, -47.62) * mm, v(-19.89, -48.1) * mm, v(-19.74, -49.53) * mm, v(-18.7, -50.87) * mm], "startDerivative": vector(-12.85, -13.04) * mm, "endDerivative": vector(18.88, -18.18) * mm});
            skFitSpline(sketch, "E63", {"points": [v(-18.7, -50.87) * mm, v(-17.28, -51.78) * mm, v(-16.07, -52.21) * mm, v(-15.26, -52.25) * mm, v(-14.4, -51.4) * mm, v(-14.78, -50.87) * mm, v(-15.04, -49.8) * mm, v(-13.85, -49.8) * mm, v(-13.06, -50.02) * mm, v(-12.42, -50.87) * mm, v(-12.03, -51.7) * mm, v(-11.34, -52.12) * mm, v(-10.66, -52.12) * mm, v(-10.58, -52.47) * mm, v(-9.4, -52.51) * mm, v(-8.41, -52) * mm, v(-8.24, -50.87) * mm, v(-7.5, -50.45) * mm, v(-7.47, -49.76) * mm, v(-8.03, -49.24) * mm, v(-8.37, -48.64) * mm, v(-7.81, -48.42) * mm, v(-7.12, -48.68) * mm, v(-6.86, -48.17) * mm, v(-6.26, -47.52) * mm, v(-6.26, -46.68) * mm, v(-6.73, -46.27) * mm, v(-6.56, -45.71) * mm, v(-7.42, -44.6) * mm, v(-7.34, -44.12) * mm, v(-6.65, -44.94) * mm, v(-5.74, -46.64) * mm, v(-5.66, -48.2) * mm, v(-6.26, -50.1) * mm, v(-6.52, -52.47) * mm, v(-6.86, -53.76) * mm, v(-8.58, -54.97) * mm, v(-10.26, -55.61) * mm, v(-11.51, -56.21) * mm, v(-12.07, -56.52) * mm], "startDerivative": vector(42.55, -30.94) * mm, "endDerivative": vector(-24.95, -13.54) * mm});
            skFitSpline(sketch, "E64", {"points": [v(-12.07, -56.52) * mm, v(-14.12, -56.74) * mm, v(-16.28, -56.63) * mm, v(-18.05, -56.52) * mm, v(-18.8, -55.78) * mm, v(-19.53, -56.06) * mm, v(-19.53, -56.52) * mm, v(-18.9, -57.89) * mm, v(-17.65, -57.94) * mm, v(-17.2, -58.34) * mm, v(-18.34, -58.92) * mm, v(-20.22, -58.46) * mm, v(-20.96, -57.72) * mm], "startDerivative": vector(-19.16, -3.23) * mm, "endDerivative": vector(-7.91, 10.3) * mm});
            skFitSpline(sketch, "E65", {"points": [v(-20.96, -57.72) * mm, v(-21.27, -56.63) * mm, v(-22.01, -56.63) * mm, v(-22.56, -57.09) * mm, v(-23.93, -57.09) * mm, v(-24.63, -55.4) * mm, v(-25.18, -54.11) * mm, v(-26.27, -54) * mm, v(-26.98, -53.53) * mm], "startDerivative": vector(-0.76, 10.76) * mm, "endDerivative": vector(-5.59, 5.6) * mm});
            skFitSpline(sketch, "E66", {"points": [v(-26.98, -53.53) * mm, v(-28.04, -49.53) * mm, v(-29.04, -47.5) * mm, v(-29.45, -47.62) * mm, v(-30.04, -47.66) * mm, v(-30.32, -47.48) * mm, v(-30.86, -47.55) * mm, v(-31.2, -47.55) * mm, v(-31.28, -47.3) * mm, v(-31.43, -47.02) * mm, v(-31.42, -46.74) * mm, v(-31.42, -46.45) * mm, v(-31.25, -46.41) * mm, v(-31.04, -46.41) * mm, v(-30.85, -46.18) * mm, v(-30.77, -46.1) * mm, v(-30.7, -45.64) * mm, v(-30.75, -45.16) * mm, v(-31.07, -44.99) * mm, v(-31.02, -44.54) * mm, v(-30.6, -44.56) * mm, v(-30.06, -44.86) * mm, v(-29.62, -45.18) * mm, v(-28.87, -44.85) * mm, v(-28.54, -44.47) * mm, v(-28.1, -43.95) * mm, v(-27.67, -43.8) * mm, v(-27.08, -43.75) * mm, v(-26.5, -43.22) * mm, v(-26.2, -42.83) * mm, v(-26.17, -42.23) * mm, v(-26.23, -41.94) * mm], "startDerivative": vector(-10.34, 44.4) * mm, "endDerivative": vector(-2.68, 10.3) * mm});
            skFitSpline(sketch, "E67", {"points": [v(-26.23, -41.94) * mm, v(-26, -41.41) * mm, v(-25.08, -40.54) * mm, v(-24.3, -39.76) * mm, v(-24.06, -39.28) * mm, v(-24.88, -39.25) * mm, v(-25.61, -39.12) * mm, v(-25.96, -39.05) * mm, v(-26, -38.62) * mm, v(-25.5, -38.46) * mm, v(-25.86, -38.32) * mm, v(-26, -38.06) * mm, v(-25.98, -37.61) * mm, v(-25.22, -37.51) * mm, v(-24.3, -37.6) * mm, v(-23.98, -37.58) * mm, v(-23.83, -37.25) * mm, v(-23.53, -36.9) * mm, v(-23.32, -36.32) * mm, v(-23.15, -35.65) * mm, v(-23.02, -34.97) * mm, v(-22.5, -34.4) * mm], "startDerivative": vector(3.32, 10.94) * mm, "endDerivative": vector(11.42, 10) * mm});
            skFitSpline(sketch, "E68", {"points": [v(-22.5, -34.4) * mm, v(-20.73, -33.38) * mm, v(-18.6, -32.28) * mm, v(-16.52, -31.14) * mm, v(-15.7, -30.47) * mm, v(-15.5, -29.33) * mm, v(-15.81, -28.77) * mm, v(-15.85, -28.03) * mm, v(-15.73, -27.2) * mm, v(-15.3, -26.96) * mm, v(-14.75, -26.6) * mm, v(-14.79, -26.1) * mm, v(-15.14, -25.47) * mm, v(-15.81, -25.07) * mm, v(-16.36, -24.84) * mm, v(-16.97, -24.55) * mm], "startDerivative": vector(17.95, 10.53) * mm, "endDerivative": vector(-11.16, 5.43) * mm});
            skFitSpline(sketch, "E69", {"points": [v(-18.25, -25.07) * mm, v(-17.78, -25.07) * mm, v(-17.3, -25.39) * mm, v(-16.87, -25.98) * mm, v(-16.64, -26.41) * mm, v(-16.52, -27.55) * mm, v(-16.87, -28.42) * mm, v(-17.27, -28.77) * mm, v(-18.25, -28.93) * mm, v(-18.8, -28.77) * mm, v(-18.64, -28.1) * mm, v(-18.6, -27.44) * mm, v(-18.37, -26.96) * mm, v(-18.49, -26.3) * mm, v(-18.49, -25.67) * mm, v(-18.25, -25.07) * mm]});
            skSolve(sketch);
        }
        {
            var Q0;
            Q0=makeQuery(id+"F0.imprint","IMPRINT",FACE,{"disambiguationData":[TD([[makeQuery(id+"F0.imprint","IMPRINT",EDGE,{"derivedFrom":sQuery(id+"F0.wireOp",EDGE,"E26")}),1.0]])]});
            var Q1;
            Q1=makeQuery(id+"F0.imprint","IMPRINT",FACE,{"disambiguationData":[TD([[makeQuery(id+"F0.imprint","IMPRINT",EDGE,{"derivedFrom":sQuery(id+"F0.wireOp",EDGE,"E53")}),-1.0]])]});
            var Q2;
            Q2=makeQuery(id+"F0.imprint","IMPRINT",FACE,{"disambiguationData":[TD([[makeQuery(id+"F0.imprint","IMPRINT",EDGE,{"derivedFrom":sQuery(id+"F0.wireOp",EDGE,"E59")}),-1.0]])]});
            var Q3;
            Q3=makeQuery(id+"F0.imprint","IMPRINT",FACE,{"disambiguationData":[TD([[makeQuery(id+"F0.imprint","IMPRINT",EDGE,{"derivedFrom":sQuery(id+"F0.wireOp",EDGE,"E69")}),-1.0]])]});
            var Q4;
            Q4=makeQuery(id+"F0.imprint","IMPRINT",FACE,{"disambiguationData":[TD([[makeQuery(id+"F0.imprint","IMPRINT",EDGE,{"derivedFrom":sQuery(id+"F0.wireOp",EDGE,"E0")}),-1.0]])]});
            var Q5;
            Q5=makeQuery(id+"F0.imprint","IMPRINT",FACE,{"disambiguationData":[TD([[makeQuery(id+"F0.imprint","IMPRINT",EDGE,{"derivedFrom":sQuery(id+"F0.wireOp",EDGE,"E0")}),-1.0]])]});
            extrude(context, id + "F1", {"entities" : qUnion([Q0, Q1, Q2, Q3, Q4, Q5]), "depth" : 10.16 * mm});
        }
        {
            var Q0;
            Q0=makeQuery(id+"F0.imprint","IMPRINT",FACE,{"disambiguationData":[TD([[makeQuery(id+"F0.imprint","IMPRINT",EDGE,{"derivedFrom":sQuery(id+"F0.wireOp",EDGE,"E47")}),1.0]])]});
            extrude(context, id + "F2", {"entities" : qUnion([Q0]), "depth" : 10.16 * mm});
        }
        {
            var Q0;
            Q0=qCreatedBy(makeId("Top.planeOp"),FACE);
            var sketch = newSketch(context, id + "F3", { "sketchPlane" : qUnion([Q0])});
            skCircle(sketch, "E70", {"center": v(-13.89, -6.21) * mm, "radius": 55.36 * mm});
            skSolve(sketch);
        }
        {
            var Q0;
            Q0=makeQuery(id+"F3.imprint","IMPRINT",FACE,{"disambiguationData":[TD([[makeQuery(id+"F3.imprint","IMPRINT",EDGE,{"derivedFrom":sQuery(id+"F3.wireOp",EDGE,"E70")}),1.0]])]});
            extrude(context, id + "F4", {"entities" : qUnion([Q0]), "depth" : 5.08 * mm});
        }
    });
